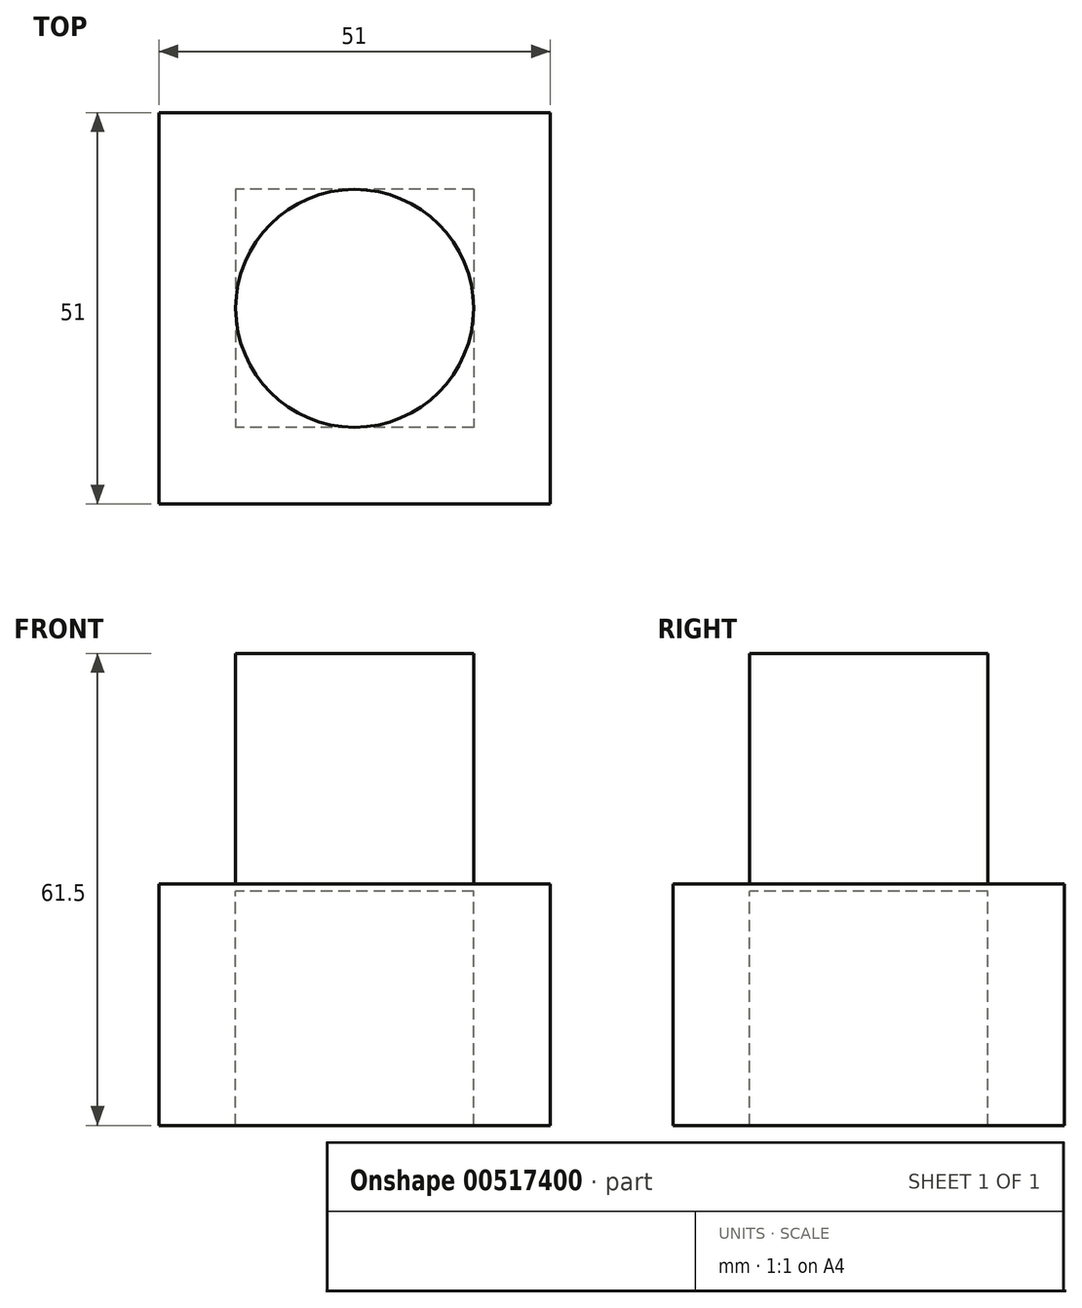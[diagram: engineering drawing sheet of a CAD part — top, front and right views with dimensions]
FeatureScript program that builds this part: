
annotation { "Feature Type Name" : "Feature", "Feature Type Description" : "" }
export const myFeature = defineFeature(function(context is Context, id is Id, definition is map)
    precondition{}
    {
        {
            var Q0;
            Q0=qCreatedBy(makeId("Top.planeOp"),FACE);
            var sketch = newSketch(context, id + "F0", { "sketchPlane" : qUnion([Q0])});
            skCircle(sketch, "E0", {"center": v(0, 0) * mm, "radius": 15.5 * mm});
            skSolve(sketch);
        }
        {
            var Q0;
            Q0=makeQuery(id+"F0.imprint","IMPRINT",FACE,{"disambiguationData":[TD([[makeQuery(id+"F0.imprint","IMPRINT",EDGE,{"derivedFrom":sQuery(id+"F0.wireOp",EDGE,"E0")}),1.0]])]});
            extrude(context, id + "F1", {"entities" : qUnion([Q0]), "depth" : 30 * mm, "offsetDistance" : 25 * mm});
        }
        {
            var Q0;
            Q0=makeQuery(id+"F1.opExtrude","CAP_FACE",FACE,{"disambiguationData":[OSD([sQuery(id+"F0.wireOp",EDGE,"E0")])],"isStart":true});
            var sketch = newSketch(context, id + "F2", { "sketchPlane" : qUnion([Q0])});
            skLineSegment(sketch, "E1.bottom", {"start": v(25.5, 25.5) * mm, "end": v(-25.5, 25.5) * mm});
            skLineSegment(sketch, "E1.top", {"start": v(25.5, -25.5) * mm, "end": v(-25.5, -25.5) * mm});
            skLineSegment(sketch, "E1.left", {"start": v(25.5, 25.5) * mm, "end": v(25.5, -25.5) * mm});
            skLineSegment(sketch, "E1.right", {"start": v(-25.5, 25.5) * mm, "end": v(-25.5, -25.5) * mm});
            skPoint(sketch, "E1.middle", {"position": v(0, 0) * mm});
            skLineSegment(sketch, "E2.bottom", {"start": v(15.5, -15.5) * mm, "end": v(-15.5, -15.5) * mm});
            skLineSegment(sketch, "E2.top", {"start": v(15.5, 15.5) * mm, "end": v(-15.5, 15.5) * mm});
            skLineSegment(sketch, "E2.left", {"start": v(15.5, -15.5) * mm, "end": v(15.5, 15.5) * mm});
            skLineSegment(sketch, "E2.right", {"start": v(-15.5, -15.5) * mm, "end": v(-15.5, 15.5) * mm});
            skSolve(sketch);
        }
        {
            var Q0;
            {var subQ0=sQuery(id+"F2.wireOp",EDGE,"E2.right");var subQ1=sQuery(id+"F2.wireOp",EDGE,"E2.top");var subQ2=makeQuery(id+"F2.imprint","INTERSECT",VERTEX,{"derivedFrom":[subQ1,subQ0]});Q0=makeQuery(id+"F2.imprint","IMPRINT",FACE,{"disambiguationData":[TD([[makeQuery(id+"F2.imprint","IMPRINT",EDGE,{"disambiguationData":[TD([[subQ2,1.0]])],"derivedFrom":subQ1}),1.0]])]});}
            var Q1;
            {var subQ0=sQuery(id+"F2.wireOp",EDGE,"E2.left");var subQ1=sQuery(id+"F2.wireOp",EDGE,"E2.top");var subQ2=makeQuery(id+"F2.imprint","INTERSECT",VERTEX,{"derivedFrom":[subQ1,subQ0]});Q1=makeQuery(id+"F2.imprint","IMPRINT",FACE,{"disambiguationData":[TD([[makeQuery(id+"F2.imprint","IMPRINT",EDGE,{"disambiguationData":[TD([[subQ2,-1.0]])],"derivedFrom":subQ1}),1.0]])]});}
            var Q2;
            {var subQ0=sQuery(id+"F2.wireOp",EDGE,"E2.left");var subQ1=sQuery(id+"F2.wireOp",EDGE,"E2.bottom");var subQ2=makeQuery(id+"F2.imprint","INTERSECT",VERTEX,{"derivedFrom":[subQ1,subQ0]});Q2=makeQuery(id+"F2.imprint","IMPRINT",FACE,{"disambiguationData":[TD([[makeQuery(id+"F2.imprint","IMPRINT",EDGE,{"disambiguationData":[TD([[subQ2,-1.0]])],"derivedFrom":subQ1}),-1.0]])]});}
            var Q3;
            {var subQ0=sQuery(id+"F2.wireOp",EDGE,"E2.right");var subQ1=sQuery(id+"F2.wireOp",EDGE,"E2.bottom");var subQ2=makeQuery(id+"F2.imprint","INTERSECT",VERTEX,{"derivedFrom":[subQ1,subQ0]});Q3=makeQuery(id+"F2.imprint","IMPRINT",FACE,{"disambiguationData":[TD([[makeQuery(id+"F2.imprint","IMPRINT",EDGE,{"disambiguationData":[TD([[subQ2,1.0]])],"derivedFrom":subQ1}),-1.0]])]});}
            var Q4;
            {var subQ1=makeQuery(id+"F1.opExtrude","CAP_EDGE",EDGE,{"disambiguationData":[OSD([sQuery(id+"F0.wireOp",EDGE,"E0")])],"isStart":true});var subQ10=sQuery(id+"F2.wireOp",EDGE,"E2.bottom");var subQ11=makeQuery(id+"F2.imprint","INTERSECT",VERTEX,{"disambiguationData":[OD(0.0)],"derivedFrom":[subQ1,subQ10]});Q4=makeQuery(id+"F2.imprint","IMPRINT",FACE,{"disambiguationData":[TD([[makeQuery(id+"F2.imprint","IMPRINT",EDGE,{"disambiguationData":[TD([[subQ11,-1.0]])],"derivedFrom":subQ10}),-1.0]])]});}
            var Q5;
            {var subQ0=sQuery(id+"F2.wireOp",EDGE,"E2.right");var subQ1=makeQuery(id+"F1.opExtrude","CAP_EDGE",EDGE,{"disambiguationData":[OSD([sQuery(id+"F0.wireOp",EDGE,"E0")])],"isStart":true});var subQ2=makeQuery(id+"F2.imprint","INTERSECT",VERTEX,{"disambiguationData":[OD(0.0)],"derivedFrom":[subQ1,subQ0]});Q5=makeQuery(id+"F2.imprint","IMPRINT",FACE,{"disambiguationData":[TD([[makeQuery(id+"F2.imprint","IMPRINT",EDGE,{"disambiguationData":[TD([[subQ2,-1.0]])],"derivedFrom":subQ0}),1.0]])]});}
            var Q6;
            {var subQ0=sQuery(id+"F2.wireOp",EDGE,"E2.top");var subQ1=makeQuery(id+"F1.opExtrude","CAP_EDGE",EDGE,{"disambiguationData":[OSD([sQuery(id+"F0.wireOp",EDGE,"E0")])],"isStart":true});var subQ2=makeQuery(id+"F2.imprint","INTERSECT",VERTEX,{"disambiguationData":[OD(0.0)],"derivedFrom":[subQ1,subQ0]});Q6=makeQuery(id+"F2.imprint","IMPRINT",FACE,{"disambiguationData":[TD([[makeQuery(id+"F2.imprint","IMPRINT",EDGE,{"disambiguationData":[TD([[subQ2,-1.0]])],"derivedFrom":subQ0}),-1.0]])]});}
            var Q7;
            {var subQ0=sQuery(id+"F2.wireOp",EDGE,"E2.bottom");var subQ1=makeQuery(id+"F1.opExtrude","CAP_EDGE",EDGE,{"disambiguationData":[OSD([sQuery(id+"F0.wireOp",EDGE,"E0")])],"isStart":true});var subQ2=makeQuery(id+"F2.imprint","INTERSECT",VERTEX,{"disambiguationData":[OD(0.0)],"derivedFrom":[subQ1,subQ0]});Q7=makeQuery(id+"F2.imprint","IMPRINT",FACE,{"disambiguationData":[TD([[makeQuery(id+"F2.imprint","IMPRINT",EDGE,{"disambiguationData":[TD([[subQ2,-1.0]])],"derivedFrom":subQ0}),1.0]])]});}
            var Q8;
            Q8=makeQuery(id+"F2.imprint","IMPRINT",FACE,{"disambiguationData":[TD([[makeQuery(id+"F2.imprint","IMPRINT",EDGE,{"derivedFrom":sQuery(id+"F2.wireOp",EDGE,"E1.bottom")}),1.0]])]});
            var Q9;
            {var subQ0=sQuery(id+"F2.wireOp",EDGE,"E2.left");var subQ1=makeQuery(id+"F1.opExtrude","CAP_EDGE",EDGE,{"disambiguationData":[OSD([sQuery(id+"F0.wireOp",EDGE,"E0")])],"isStart":true});var subQ2=makeQuery(id+"F2.imprint","INTERSECT",VERTEX,{"disambiguationData":[OD(0.0)],"derivedFrom":[subQ1,subQ0]});Q9=makeQuery(id+"F2.imprint","IMPRINT",FACE,{"disambiguationData":[TD([[makeQuery(id+"F2.imprint","IMPRINT",EDGE,{"disambiguationData":[TD([[subQ2,-1.0]])],"derivedFrom":subQ0}),-1.0]])]});}
            var Q10;
            {var subQ0=makeQuery(id+"F1.opExtrude","CAP_EDGE",EDGE,{"disambiguationData":[OSD([sQuery(id+"F0.wireOp",EDGE,"E0")])],"isStart":true});var subQ1=makeQuery(id+"F2.imprint","INTERSECT",VERTEX,{"derivedFrom":[subQ0,sQuery(id+"F2.wireOp",EDGE,"E2.bottom")]});Q10=makeQuery(id+"F2.imprint","IMPRINT",FACE,{"disambiguationData":[TD([[makeQuery(id+"F2.imprint","IMPRINT",EDGE,{"disambiguationData":[TD([[subQ1,1.0]])],"derivedFrom":subQ0}),-1.0]])]});}
            extrude(context, id + "F3", {"entities" : qUnion([Q0, Q1, Q2, Q3, Q4, Q5, Q6, Q7, Q8, Q9, Q10]), "operationType" : NewBodyOperationType.ADD, "depth" : 1 * mm, "offsetDistance" : 25 * mm});
        }
        {
            var Q0;
            Q0=makeQuery(id+"F3.opExtrude","CAP_FACE",FACE,{"disambiguationData":[OSD([sQuery(id+"F2.wireOp",EDGE,"E1.bottom"),sQuery(id+"F2.wireOp",EDGE,"E1.top"),sQuery(id+"F2.wireOp",EDGE,"E1.left"),sQuery(id+"F2.wireOp",EDGE,"E1.right")])],"isStart":false});
            var sketch = newSketch(context, id + "F4", { "sketchPlane" : qUnion([Q0])});
            skLineSegment(sketch, "E3.0", {"start": v(25.5, 25.5) * mm, "end": v(-25.5, 25.5) * mm});
            skLineSegment(sketch, "E4.0", {"start": v(15.5, 15.5) * mm, "end": v(-15.5, 15.5) * mm});
            skLineSegment(sketch, "E5.0", {"start": v(15.5, -15.5) * mm, "end": v(15.5, 15.5) * mm});
            skLineSegment(sketch, "E6.0", {"start": v(15.5, -15.5) * mm, "end": v(-15.5, -15.5) * mm});
            skLineSegment(sketch, "E7.0", {"start": v(-15.5, -15.5) * mm, "end": v(-15.5, 15.5) * mm});
            skLineSegment(sketch, "E8.0", {"start": v(-25.5, 25.5) * mm, "end": v(-25.5, -25.5) * mm});
            skLineSegment(sketch, "E9.0", {"start": v(25.5, -25.5) * mm, "end": v(-25.5, -25.5) * mm});
            skLineSegment(sketch, "E10.0", {"start": v(25.5, 25.5) * mm, "end": v(25.5, -25.5) * mm});
            skSolve(sketch);
        }
        {
            var Q0;
            Q0=makeQuery(id+"F4.imprint","IMPRINT",FACE,{"disambiguationData":[TD([[makeQuery(id+"F4.imprint","IMPRINT",EDGE,{"derivedFrom":sQuery(id+"F4.wireOp",EDGE,"E3.0")}),1.0]])]});
            extrude(context, id + "F5", {"entities" : qUnion([Q0]), "operationType" : NewBodyOperationType.ADD, "depth" : 30.5 * mm, "offsetDistance" : 25 * mm});
        }
    });
